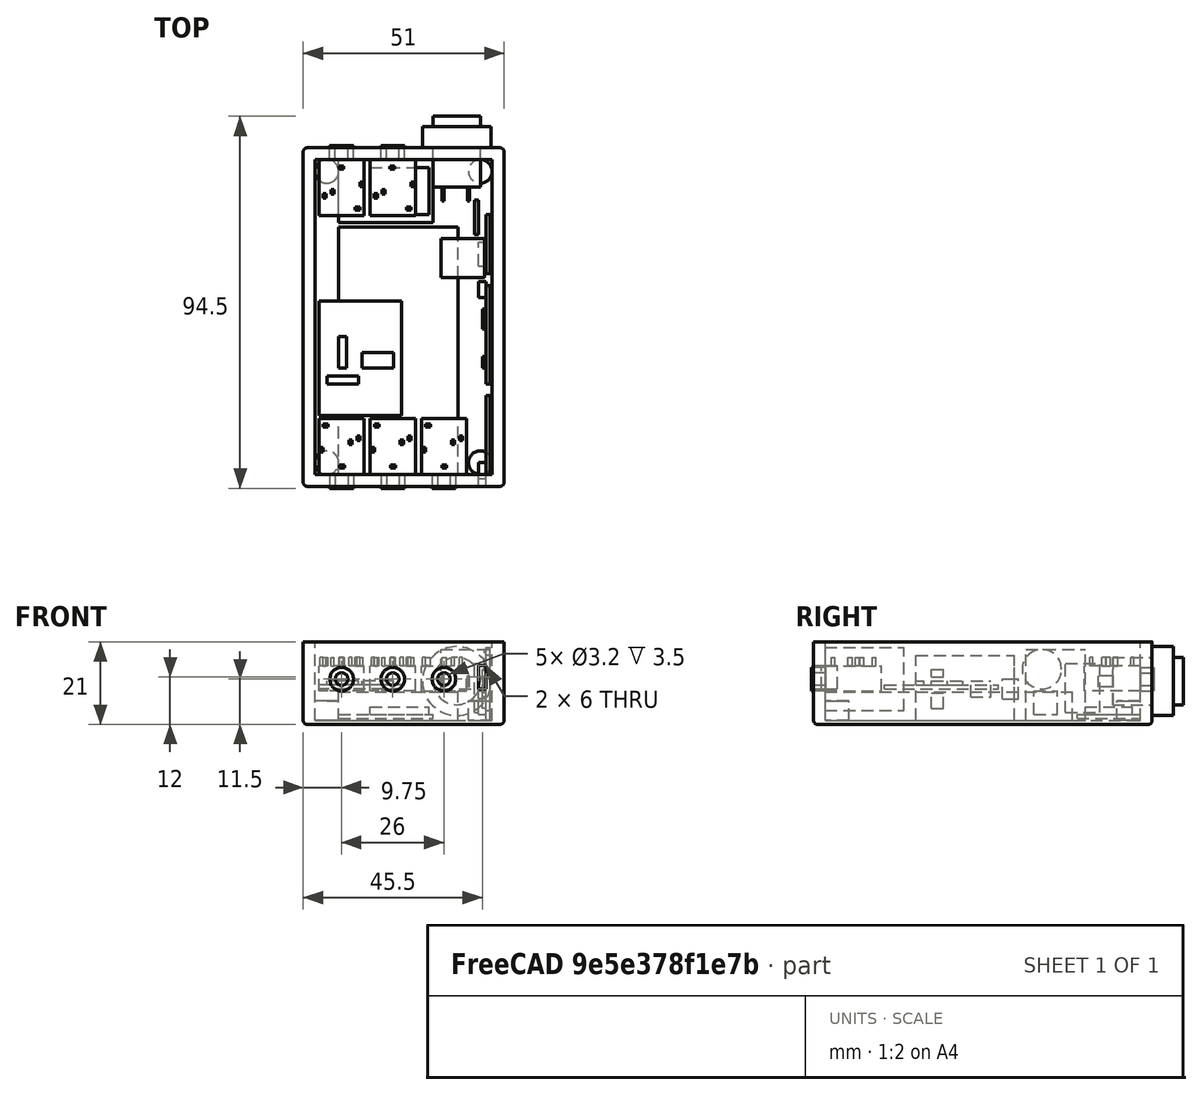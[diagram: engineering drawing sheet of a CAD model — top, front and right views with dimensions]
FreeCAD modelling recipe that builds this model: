
FCSTD DOCUMENT  (FreeCAD 0.15R4671 (Git))
Label: Gehäuse-Zeichnung
License: All rights reserved
LicenseURL: http://en.wikipedia.org/wiki/All_rights_reserved
objects: Part::Box×52, Part::Cylinder×17, Part::MultiFuse×11, Part::Cut×7, Part::Fillet×1
note: 88 computed .brp shape members not serialized (recipe doc carries the construction recipe); baked Part::Feature solids carry a one-line shape summary decoded from their .brp

FEATURE [Part::Box] Box  label="Würfel"
  Height = 21
  Length = 51
  Width = 86
FEATURE [Part::Box] Box001  label="Würfel001"
  Height = 20
  Length = 45
  Placement = pos=(3,3,1) rot=(0,0,1;0rad)
  Width = 80
FEATURE [Part::Cut] Cut  label="GehäuseGrund"
  Base = -> Box
  Tool = -> Box001
FEATURE [Part::Box] Box002  label="Akku"
  Height = 7.3
  Length = 30.3
  Placement = pos=(9,3,1) rot=(0,0,1;0rad)
  Width = 62.8
FEATURE [Part::Cylinder] Cylinder  label="Montageloch1"
  Angle = 360
  Height = 5
  Placement = pos=(6,6,1) rot=(0,0,1;0rad)
  Radius = 3
FEATURE [Part::Cylinder] Cylinder001  label="Montageloch2"
  Angle = 360
  Height = 5
  Placement = pos=(45,6,1) rot=(0,0,1;0rad)
  Radius = 3
FEATURE [Part::Cylinder] Cylinder002  label="Montageloch3"
  Angle = 360
  Height = 5
  Placement = pos=(6,80,1) rot=(0,0,1;0rad)
  Radius = 3
FEATURE [Part::Cylinder] Cylinder003  label="Montageloch4"
  Angle = 360
  Height = 5
  Placement = pos=(45,80,1) rot=(0,0,1;0rad)
  Radius = 3
FEATURE [Part::Box] Box003  label="ESP-Platine"
  Height = 1
  Length = 24
  Placement = pos=(9,67,1) rot=(0,0,1;0rad)
  Width = 16
FEATURE [Part::Box] Box004  label="ESP-Blechabdeckung"
  Height = 2
  Length = 15
  Placement = pos=(17,69,2) rot=(0,0,1;0rad)
  Width = 12
FEATURE [Part::MultiFuse] Fusion  label="ESP-12E/F"
  Placement = pos=(0,0,0.5) rot=(0,0,1;0rad)
  Shapes = -> [Box004,Box003]
FEATURE [Part::Box] Box006  label="Anschlusspin1"
  Height = 2.5
  Length = 1.2
  Placement = pos=(-14.9,12,6) rot=(0,0,1;0rad)
  Width = 0.8
FEATURE [Part::Box] Box008  label="Anschlusspin003"
  Height = 2.5
  Length = 1.2
  Placement = pos=(-10.75,1.6,6) rot=(0,0,1;0rad)
  Width = 0.8
FEATURE [Part::Box] Box009  label="Anschlusspin004"
  Height = 2.5
  Length = 1.2
  Placement = pos=(-7.55,7.6,6) rot=(0,0,1;1.5708rad)
  Width = 0.8
FEATURE [Part::Box] Box010  label="Anschlusspin005"
  Height = 2.5
  Length = 1.2
  Placement = pos=(-5.55,8.6,6) rot=(0,0,1;1.5708rad)
  Width = 0.8
FEATURE [Part::Box] Box011  label="Anschlusspin006"
  Height = 2.5
  Length = 1.2
  Placement = pos=(-14.9,5.7,6) rot=(0,0,1;1.5708rad)
  Width = 0.8
FEATURE [Part::Cylinder] Cylinder005  label="3,5mm Steckerloch"
  Angle = 360
  Height = 3.5
  Placement = pos=(-10.25,0,3) rot=(1,0,0;1.5708rad)
  Radius = 1.6
FEATURE [Part::Box] Box012  label="3,5mm Gehäuse"
  Height = 6.3
  Length = 11.5
  Placement = pos=(-16,0,0) rot=(0,0,1;0rad)
  Width = 14.2
FEATURE [Part::Cylinder] Cylinder006  label="Zylinder"
  Angle = 360
  Height = 3.5
  Placement = pos=(-10.25,0,3) rot=(1,0,0;1.5708rad)
  Radius = 3
FEATURE [Part::Cut] Cut001  label="Buchse"
  Base = -> Cylinder006
  Tool = -> Cylinder005
FEATURE [Part::MultiFuse] Fusion001  label="3,5mm Buchse"
  Placement = pos=(20,3,8.5) rot=(0,0,1;0rad)
  Shapes = -> [Cut001,Box012,Box009,Box006,Box011,Box010,Box008]
FEATURE [Part::Box] Box013  label="Anschlusspin007"
  Height = 2.5
  Length = 1.2
  Placement = pos=(-14.9,12,6) rot=(0,0,1;0rad)
  Width = 0.8
FEATURE [Part::Box] Box014  label="Anschlusspin008"
  Height = 2.5
  Length = 1.2
  Placement = pos=(-10.75,1.6,6) rot=(0,0,1;0rad)
  Width = 0.8
FEATURE [Part::Box] Box015  label="Anschlusspin009"
  Height = 2.5
  Length = 1.2
  Placement = pos=(-7.55,7.6,6) rot=(0,0,1;1.5708rad)
  Width = 0.8
FEATURE [Part::Box] Box016  label="Anschlusspin010"
  Height = 2.5
  Length = 1.2
  Placement = pos=(-5.55,8.6,6) rot=(0,0,1;1.5708rad)
  Width = 0.8
FEATURE [Part::Box] Box017  label="Anschlusspin011"
  Height = 2.5
  Length = 1.2
  Placement = pos=(-14.9,5.7,6) rot=(0,0,1;1.5708rad)
  Width = 0.8
FEATURE [Part::Cylinder] Cylinder007  label="3,5mm Steckerloch001"
  Angle = 360
  Height = 3.5
  Placement = pos=(-10.25,0,3) rot=(1,0,0;1.5708rad)
  Radius = 1.6
FEATURE [Part::Box] Box018  label="3,5mm Gehäuse001"
  Height = 6.3
  Length = 11.5
  Placement = pos=(-16,0,0) rot=(0,0,1;0rad)
  Width = 14.2
FEATURE [Part::Cylinder] Cylinder008  label="Zylinder001"
  Angle = 360
  Height = 3.5
  Placement = pos=(-10.25,0,3) rot=(1,0,0;1.5708rad)
  Radius = 3
FEATURE [Part::Cut] Cut002  label="Buchse001"
  Base = -> Cylinder008
  Tool = -> Cylinder007
FEATURE [Part::MultiFuse] Fusion002  label="3,5mm Buchse001"
  Placement = pos=(33,3,8.5) rot=(0,0,1;0rad)
  Shapes = -> [Cut002,Box018,Box015,Box013,Box017,Box016,Box014]
FEATURE [Part::Box] Box019  label="Anschlusspin012"
  Height = 2.5
  Length = 1.2
  Placement = pos=(-14.9,12,6) rot=(0,0,1;0rad)
  Width = 0.8
FEATURE [Part::Box] Box020  label="Anschlusspin013"
  Height = 2.5
  Length = 1.2
  Placement = pos=(-10.75,1.6,6) rot=(0,0,1;0rad)
  Width = 0.8
FEATURE [Part::Box] Box021  label="Anschlusspin014"
  Height = 2.5
  Length = 1.2
  Placement = pos=(-7.55,7.6,6) rot=(0,0,1;1.5708rad)
  Width = 0.8
FEATURE [Part::Box] Box022  label="Anschlusspin015"
  Height = 2.5
  Length = 1.2
  Placement = pos=(-5.55,8.6,6) rot=(0,0,1;1.5708rad)
  Width = 0.8
FEATURE [Part::Box] Box023  label="Anschlusspin016"
  Height = 2.5
  Length = 1.2
  Placement = pos=(-14.9,5.7,6) rot=(0,0,1;1.5708rad)
  Width = 0.8
FEATURE [Part::Cylinder] Cylinder009  label="3,5mm Steckerloch002"
  Angle = 360
  Height = 3.5
  Placement = pos=(-10.25,0,3) rot=(1,0,0;1.5708rad)
  Radius = 1.6
FEATURE [Part::Box] Box024  label="3,5mm Gehäuse002"
  Height = 6.3
  Length = 11.5
  Placement = pos=(-16,0,0) rot=(0,0,1;0rad)
  Width = 14.2
FEATURE [Part::Cylinder] Cylinder010  label="Zylinder002"
  Angle = 360
  Height = 3.5
  Placement = pos=(-10.25,0,3) rot=(1,0,0;1.5708rad)
  Radius = 3
FEATURE [Part::Cut] Cut003  label="Buchse002"
  Base = -> Cylinder010
  Tool = -> Cylinder009
FEATURE [Part::MultiFuse] Fusion003  label="3,5mm Buchse002"
  Placement = pos=(46,3,8.5) rot=(0,0,1;0rad)
  Shapes = -> [Cut003,Box024,Box021,Box019,Box023,Box022,Box020]
FEATURE [Part::Box] Box025  label="Anschlusspin017"
  Height = 2.5
  Length = 1.2
  Placement = pos=(-14.9,12,6) rot=(0,0,1;0rad)
  Width = 0.8
FEATURE [Part::Box] Box026  label="Anschlusspin018"
  Height = 2.5
  Length = 1.2
  Placement = pos=(-10.75,1.6,6) rot=(0,0,1;0rad)
  Width = 0.8
FEATURE [Part::Box] Box027  label="Anschlusspin019"
  Height = 2.5
  Length = 1.2
  Placement = pos=(-7.55,7.6,6) rot=(0,0,1;1.5708rad)
  Width = 0.8
FEATURE [Part::Box] Box028  label="Anschlusspin020"
  Height = 2.5
  Length = 1.2
  Placement = pos=(-5.55,8.6,6) rot=(0,0,1;1.5708rad)
  Width = 0.8
FEATURE [Part::Box] Box029  label="Anschlusspin021"
  Height = 2.5
  Length = 1.2
  Placement = pos=(-14.9,5.7,6) rot=(0,0,1;1.5708rad)
  Width = 0.8
FEATURE [Part::Cylinder] Cylinder011  label="3,5mm Steckerloch003"
  Angle = 360
  Height = 3.5
  Placement = pos=(-10.25,0,3) rot=(1,0,0;1.5708rad)
  Radius = 1.6
FEATURE [Part::Box] Box030  label="3,5mm Gehäuse003"
  Height = 6.3
  Length = 11.5
  Placement = pos=(-16,0,0) rot=(0,0,1;0rad)
  Width = 14.2
FEATURE [Part::Cylinder] Cylinder012  label="Zylinder003"
  Angle = 360
  Height = 3.5
  Placement = pos=(-10.25,0,3) rot=(1,0,0;1.5708rad)
  Radius = 3
FEATURE [Part::Cut] Cut004  label="Buchse003"
  Base = -> Cylinder012
  Tool = -> Cylinder011
FEATURE [Part::MultiFuse] Fusion004  label="3,5mm Buchse003"
  Placement = pos=(-0.5,83,8.5) rot=(0,0,1;3.14159rad)
  Shapes = -> [Cut004,Box030,Box027,Box025,Box029,Box028,Box026]
FEATURE [Part::Box] Box031  label="Anschlusspin022"
  Height = 2.5
  Length = 1.2
  Placement = pos=(-14.9,12,6) rot=(0,0,1;0rad)
  Width = 0.8
FEATURE [Part::Box] Box032  label="Anschlusspin023"
  Height = 2.5
  Length = 1.2
  Placement = pos=(-10.75,1.6,6) rot=(0,0,1;0rad)
  Width = 0.8
FEATURE [Part::Box] Box033  label="Anschlusspin024"
  Height = 2.5
  Length = 1.2
  Placement = pos=(-7.55,7.6,6) rot=(0,0,1;1.5708rad)
  Width = 0.8
FEATURE [Part::Box] Box034  label="Anschlusspin025"
  Height = 2.5
  Length = 1.2
  Placement = pos=(-5.55,8.6,6) rot=(0,0,1;1.5708rad)
  Width = 0.8
FEATURE [Part::Box] Box035  label="Anschlusspin026"
  Height = 2.5
  Length = 1.2
  Placement = pos=(-14.9,5.7,6) rot=(0,0,1;1.5708rad)
  Width = 0.8
FEATURE [Part::Cylinder] Cylinder013  label="3,5mm Steckerloch004"
  Angle = 360
  Height = 3.5
  Placement = pos=(-10.25,0,3) rot=(1,0,0;1.5708rad)
  Radius = 1.6
FEATURE [Part::Box] Box036  label="3,5mm Gehäuse004"
  Height = 6.3
  Length = 11.5
  Placement = pos=(-16,0,0) rot=(0,0,1;0rad)
  Width = 14.2
FEATURE [Part::Cylinder] Cylinder014  label="Zylinder004"
  Angle = 360
  Height = 3.5
  Placement = pos=(-10.25,0,3) rot=(1,0,0;1.5708rad)
  Radius = 3
FEATURE [Part::Cut] Cut005  label="Buchse004"
  Base = -> Cylinder014
  Tool = -> Cylinder013
FEATURE [Part::MultiFuse] Fusion005  label="3,5mm Buchse004"
  Placement = pos=(12.5,83,8.5) rot=(0,0,1;3.14159rad)
  Shapes = -> [Cut005,Box036,Box033,Box031,Box035,Box034,Box032]
FEATURE [Part::Cylinder] Cylinder015  label="Zylinder005"
  Angle = 360
  Height = 18
  Placement = pos=(-20,0,0) rot=(1,0,0;1.5708rad)
  Radius = 6
FEATURE [Part::Cylinder] Cylinder016  label="Zylinder006"
  Angle = 360
  Height = 5.5
  Placement = pos=(-20,-9.9,0) rot=(1,0,0;1.5708rad)
  Radius = 8.75
FEATURE [Part::Box] Box037  label="Anschluss"
  Height = 2.8
  Length = 0.5
  Placement = pos=(-16.8,0,-1.5) rot=(0,0,1;0rad)
  Width = 3.6
FEATURE [Part::Box] Box038  label="Anschluss001"
  Height = 2.8
  Length = 0.5
  Placement = pos=(-23.3,0,-1.5) rot=(0,0,1;0rad)
  Width = 3.6
FEATURE [Part::MultiFuse] Fusion006  label="Taster"
  Placement = pos=(19,76,11) rot=(0,0,1;3.14159rad)
  Shapes = -> [Cylinder015,Cylinder016,Box037,Box038]
FEATURE [Part::Box] Box039  label="Widerstände"
  Height = 1
  Length = 8
  Placement = pos=(15,32,9.5) rot=(0,0,1;0rad)
  Width = 2
FEATURE [Part::Box] Box040  label="Platine003"
  Height = 1
  Length = 29
  Placement = pos=(3,18,8.5) rot=(0,0,1;0rad)
  Width = 21
FEATURE [Part::Box] Box041  label="Treiberchip001"
  Height = 1
  Length = 4
  Placement = pos=(15,20,9.5) rot=(0,0,1;0rad)
  Width = 8
FEATURE [Part::Box] Box042  label="LEDs (optional deaktiviert)"
  Height = 1
  Length = 2
  Placement = pos=(11,29,9.5) rot=(0,0,1;0rad)
  Width = 8
FEATURE [Part::MultiFuse] Fusion007  label="Treiberplatine"
  Placement = pos=(43,15,0.5) rot=(0,0,1;1.5708rad)
  Shapes = -> [Box039,Box040,Box041,Box042]
FEATURE [Part::Box] Box043  label="Platine4"
  Height = 1
  Length = 16.5
  Placement = pos=(26,18,8.5) rot=(0,0,1;0rad)
  Width = 25
FEATURE [Part::Box] Box044  label="Ladechip"
  Height = 1
  Length = 4
  Placement = pos=(32,32,9.5) rot=(0,0,1;0rad)
  Width = 5
FEATURE [Part::Box] Box045  label="MicroUSB"
  Height = 2
  Length = 5
  Placement = pos=(31.5,40,9.5) rot=(0,0,1;0rad)
  Width = 4
FEATURE [Part::Box] Box046  label="Ladechip001"
  Height = 1
  Length = 4
  Placement = pos=(29,22,9.5) rot=(0,0,1;0rad)
  Width = 3
FEATURE [Part::Box] Box047  label="Ladechip002"
  Height = 1
  Length = 2
  Placement = pos=(37,22,9.5) rot=(0,0,1;0rad)
  Width = 3
FEATURE [Part::MultiFuse] Fusion008  label="Ladeplatine"
  Placement = pos=(56,8,-25) rot=(0,-1,0;1.5708rad)
  Shapes = -> [Box043,Box044,Box045,Box047,Box046]
FEATURE [Part::Box] Box048  label="Platine5"
  Height = 16
  Length = 1
  Placement = pos=(47,3,3.5) rot=(0,0,1;0rad)
  Width = 20
FEATURE [Part::Box] Box049  label="MicroUSB001"
  Height = 6
  Length = 2
  Placement = pos=(45,2,9) rot=(0,0,1;0rad)
  Width = 4
FEATURE [Part::Box] Box050  label="MicroUSB002"
  Height = 6
  Length = 2
  Placement = pos=(44.5,0,9) rot=(0,0,1;0rad)
  Width = 4
FEATURE [Part::Cut] Cut006  label="Gehäuse1"
  Base = -> Cut
  Tool = -> Box050
FEATURE [Part::MultiFuse] Fusion009  label="Programmieradapter"
  Placement = pos=(-0.5,0,0) rot=(0,0,1;0rad)
  Shapes = -> [Box049,Box048]
FEATURE [Part::Fillet] Fillet  label="Gehäuse3"
  Base = -> Cut006
  Edges = 8 edges r=1: [Edge1,Edge3,Edge4,Edge5,Edge6,Edge18,Edge19,Edge20]
FEATURE [Part::MultiFuse] Fusion010  label="Gehäuse"
  Shapes = -> [Fillet,Cylinder003,Cylinder002,Cylinder001,Cylinder]
FEATURE [Part::Box] Box051  label="Platine004"
  Height = 18
  Length = 1
  Placement = pos=(46.5,54,1) rot=(0,0,1;0rad)
  Width = 15
FEATURE [Part::Box] Box052  label="HauptFET"
  Height = 6
  Length = 2
  Placement = pos=(44.5,56,2.5) rot=(0,0,1;0rad)
  Width = 6
FEATURE [Part::Box] Box053  label="Platine005"
  Height = 12.5
  Length = 1
  Placement = pos=(43.5,64,3) rot=(0,0,1;0rad)
  Width = 8.7
FEATURE [Part::Cylinder] Cylinder017  label="Zylinder007"
  Angle = 360
  Height = 11
  Placement = pos=(35,58,14) rot=(0,1,0;1.5708rad)
  Radius = 5
